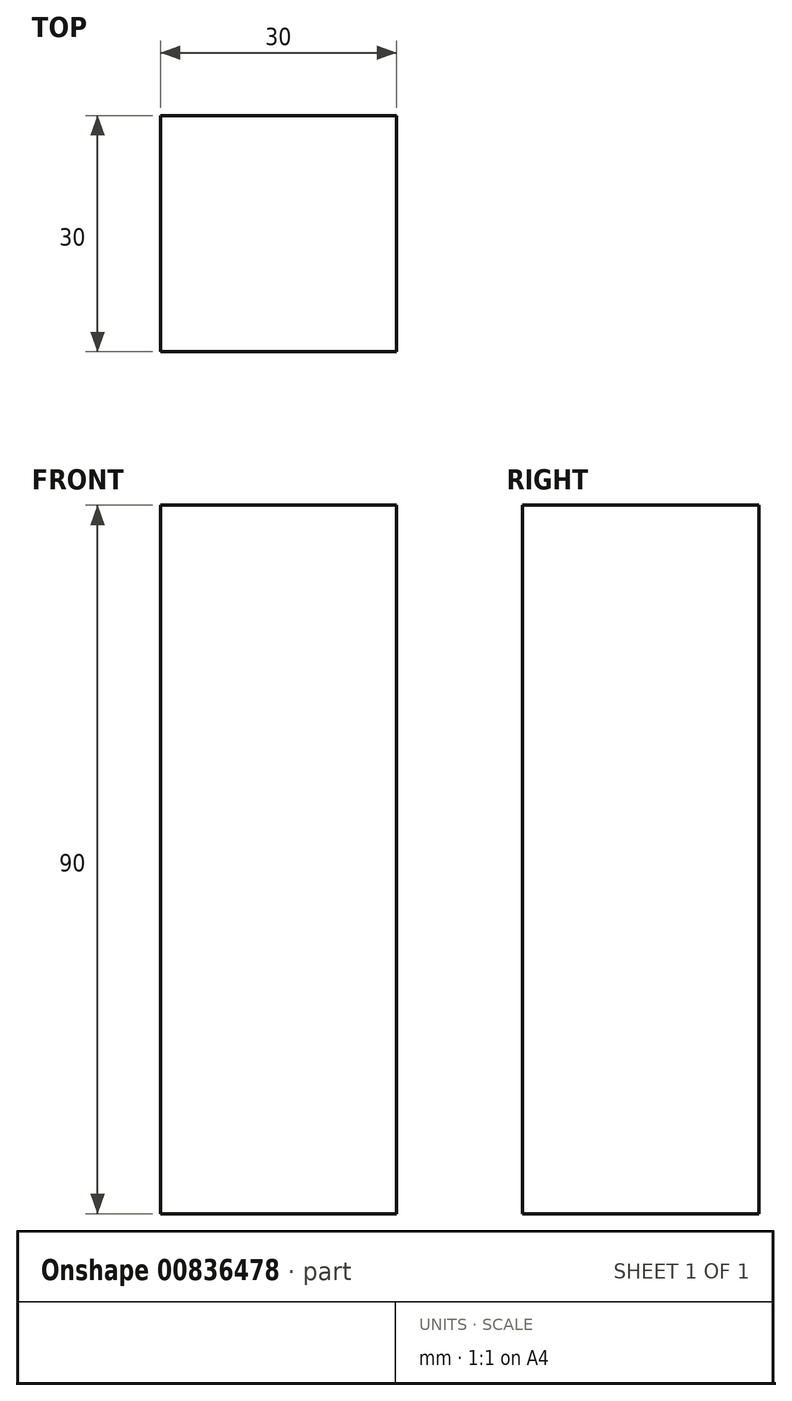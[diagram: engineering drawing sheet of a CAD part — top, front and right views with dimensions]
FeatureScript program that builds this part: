
annotation { "Feature Type Name" : "Feature", "Feature Type Description" : "" }
export const myFeature = defineFeature(function(context is Context, id is Id, definition is map)
    precondition{}
    {
        {
            var Q0;
            Q0=qCreatedBy(makeId("Top.planeOp"),FACE);
            var sketch = newSketch(context, id + "F0", { "sketchPlane" : qUnion([Q0])});
            skLineSegment(sketch, "E0.bottom", {"start": v(-15, 15) * mm, "end": v(15, 15) * mm});
            skLineSegment(sketch, "E0.top", {"start": v(-15, -15) * mm, "end": v(15, -15) * mm});
            skLineSegment(sketch, "E0.left", {"start": v(-15, 15) * mm, "end": v(-15, -15) * mm});
            skLineSegment(sketch, "E0.right", {"start": v(15, 15) * mm, "end": v(15, -15) * mm});
            skSolve(sketch);
        }
        {
            var Q0;
            Q0=makeQuery(id+"F0.imprint","IMPRINT",FACE,{"disambiguationData":[TD([[makeQuery(id+"F0.imprint","IMPRINT",EDGE,{"derivedFrom":sQuery(id+"F0.wireOp",EDGE,"E0.bottom")}),-1.0]])]});
            extrude(context, id + "F1", {"entities" : qUnion([Q0]), "depth" : 90 * mm, "offsetDistance" : 25 * mm});
        }
    });
